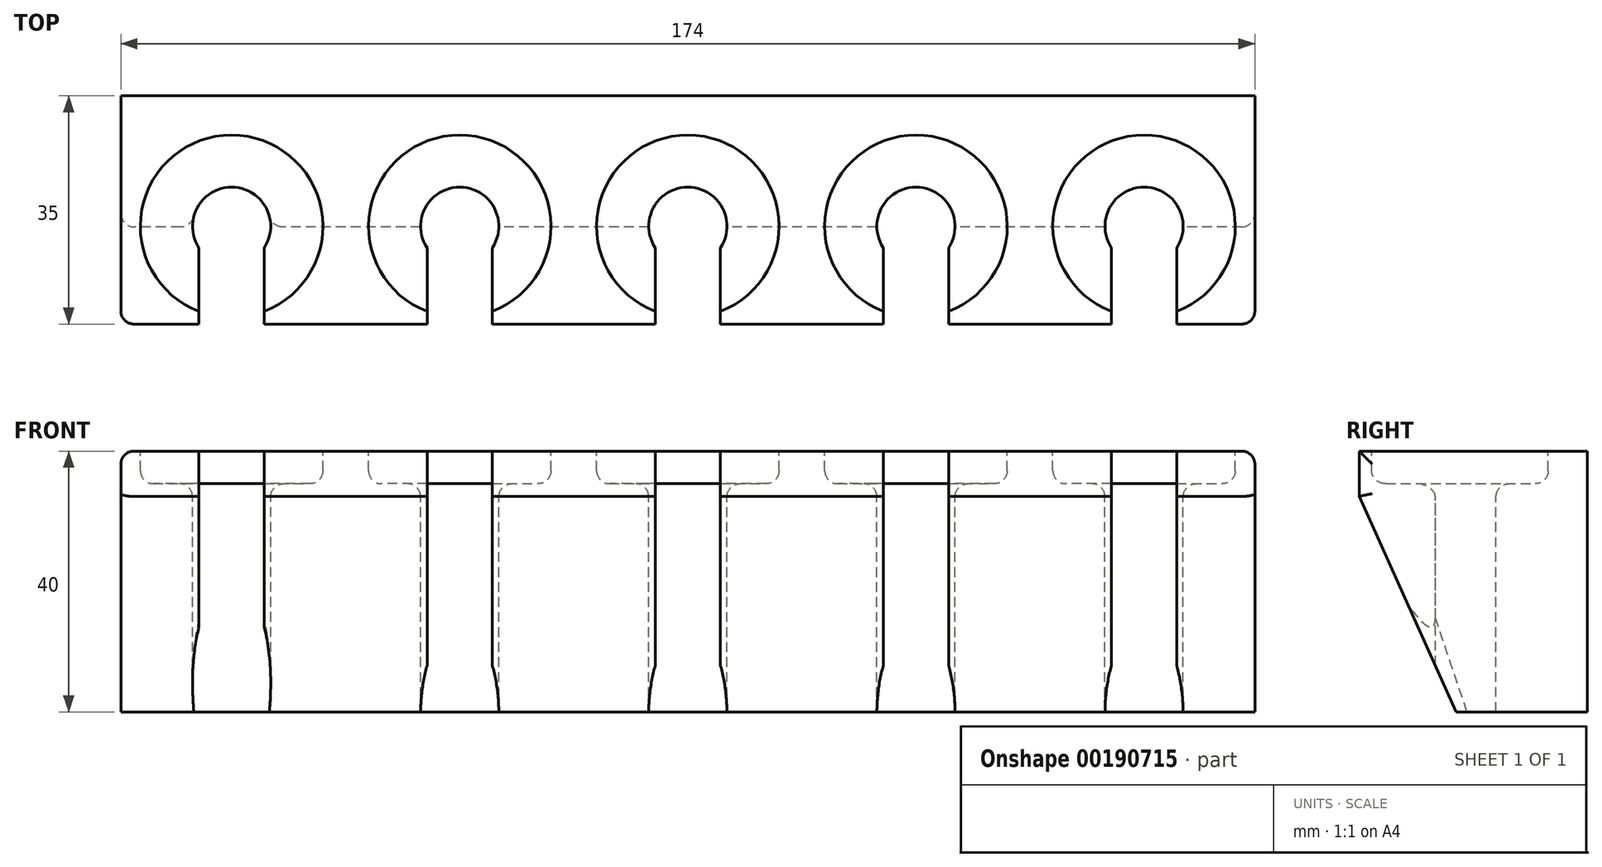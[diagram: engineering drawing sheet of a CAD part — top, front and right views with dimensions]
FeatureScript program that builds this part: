
annotation { "Feature Type Name" : "Feature", "Feature Type Description" : "" }
export const myFeature = defineFeature(function(context is Context, id is Id, definition is map)
    precondition{}
    {
        {
            var Q0;
            Q0=qCreatedBy(makeId("Right.planeOp"),FACE);
            var sketch = newSketch(context, id + "F0", { "sketchPlane" : qUnion([Q0])});
            skLineSegment(sketch, "E0", {"start": v(0, 0) * mm, "end": v(0, -40) * mm});
            skLineSegment(sketch, "E1", {"start": v(-35, 0) * mm, "end": v(0, 0) * mm});
            skLineSegment(sketch, "E2", {"start": v(-20.11, -40) * mm, "end": v(0, -40) * mm});
            skLineSegment(sketch, "E3", {"start": v(-35, 0) * mm, "end": v(-35, -6.93) * mm});
            skLineSegment(sketch, "E4", {"start": v(-35, -6.93) * mm, "end": v(-20.11, -40) * mm});
            skSolve(sketch);
        }
        {
            var Q0;
            Q0=makeQuery(id+"F0.imprint","IMPRINT",FACE,{"disambiguationData":[TD([[makeQuery(id+"F0.imprint","IMPRINT",EDGE,{"derivedFrom":sQuery(id+"F0.wireOp",EDGE,"E0")}),-1.0]])]});
            extrude(context, id + "F1", {"entities" : qUnion([Q0]), "depth" : 174 * mm});
        }
        {
            var Q0;
            Q0=makeQuery(id+"F1.opExtrude","SWEPT_FACE",FACE,{"disambiguationData":[OSD([sQuery(id+"F0.wireOp",EDGE,"E1")])]});
            var sketch = newSketch(context, id + "F2", { "sketchPlane" : qUnion([Q0])});
            skLineSegment(sketch, "E5", {"start": v(-22.77, -20) * mm, "end": v(173.52, -20) * mm, "construction": true});
            skLineSegment(sketch, "E6", {"start": v(17, 14.3) * mm, "end": v(17, -43.16) * mm, "construction": true});
            skArc(sketch, "E7", {"start": v(22, -23.32) * mm, "mid": v(17, -14) * mm, "end": v(12, -23.32) * mm});
            skLineSegment(sketch, "E8.direction1", {"start": v(17, -20) * mm, "end": v(18, -20) * mm, "construction": true});
            skLineSegment(sketch, "E9", {"start": v(12, -23.32) * mm, "end": v(12, -35) * mm});
            skLineSegment(sketch, "E10", {"start": v(12, -35) * mm, "end": v(22, -35) * mm});
            skLineSegment(sketch, "E11", {"start": v(22, -35) * mm, "end": v(22, -23.32) * mm});
            skArc(sketch, "E12.1.0.0", {"start": v(57, -23.32) * mm, "mid": v(52, -14) * mm, "end": v(47, -23.32) * mm});
            skLineSegment(sketch, "E12.1.0.1", {"start": v(47, -23.32) * mm, "end": v(47, -35) * mm});
            skLineSegment(sketch, "E12.1.0.2", {"start": v(47, -35) * mm, "end": v(57, -35) * mm});
            skLineSegment(sketch, "E12.1.0.3", {"start": v(57, -35) * mm, "end": v(57, -23.32) * mm});
            skArc(sketch, "E12.2.0.0", {"start": v(92, -23.32) * mm, "mid": v(87, -14) * mm, "end": v(82, -23.32) * mm});
            skLineSegment(sketch, "E12.2.0.1", {"start": v(82, -23.32) * mm, "end": v(82, -35) * mm});
            skLineSegment(sketch, "E12.2.0.2", {"start": v(82, -35) * mm, "end": v(92, -35) * mm});
            skLineSegment(sketch, "E12.2.0.3", {"start": v(92, -35) * mm, "end": v(92, -23.32) * mm});
            skArc(sketch, "E12.3.0.0", {"start": v(127, -23.32) * mm, "mid": v(122, -14) * mm, "end": v(117, -23.32) * mm});
            skLineSegment(sketch, "E12.3.0.1", {"start": v(117, -23.32) * mm, "end": v(117, -35) * mm});
            skLineSegment(sketch, "E12.3.0.2", {"start": v(117, -35) * mm, "end": v(127, -35) * mm});
            skLineSegment(sketch, "E12.3.0.3", {"start": v(127, -35) * mm, "end": v(127, -23.32) * mm});
            skArc(sketch, "E12.4.0.0", {"start": v(162, -23.32) * mm, "mid": v(157, -14) * mm, "end": v(152, -23.32) * mm});
            skLineSegment(sketch, "E12.4.0.1", {"start": v(152, -23.32) * mm, "end": v(152, -35) * mm});
            skLineSegment(sketch, "E12.4.0.2", {"start": v(152, -35) * mm, "end": v(162, -35) * mm});
            skLineSegment(sketch, "E12.4.0.3", {"start": v(162, -35) * mm, "end": v(162, -23.32) * mm});
            skLineSegment(sketch, "E12.direction1", {"start": v(12, -35) * mm, "end": v(47, -35) * mm, "construction": true});
            skSolve(sketch);
        }
        {
            var Q0;
            Q0 = qSketchRegion(id + "F2", true);
            extrude(context, id + "F3", {"entities" : qUnion([Q0]), "operationType" : NewBodyOperationType.REMOVE, "endBound" : BoundingType.THROUGH_ALL, "oppositeDirection" : true, "depth" : 25 * mm});
        }
        {
            var Q0;
            Q0=makeQuery(id+"F2.imprint","IMPRINT",FACE,{"disambiguationData":[TD([[makeQuery(id+"F2.imprint","IMPRINT",EDGE,{"derivedFrom":sQuery(id+"F2.wireOp",EDGE,"E7")}),-1.0]])]});
            var sketch = newSketch(context, id + "F4", { "sketchPlane" : qUnion([Q0])});
            skPoint(sketch, "E13.0", {"position": v(17, -20) * mm});
            skCircle(sketch, "E14", {"center": v(17, -20) * mm, "radius": 14 * mm});
            skCircle(sketch, "E15.1.0.0", {"center": v(52, -20) * mm, "radius": 14 * mm});
            skCircle(sketch, "E15.2.0.0", {"center": v(87, -20) * mm, "radius": 14 * mm});
            skCircle(sketch, "E15.3.0.0", {"center": v(122, -20) * mm, "radius": 14 * mm});
            skCircle(sketch, "E15.4.0.0", {"center": v(157, -20) * mm, "radius": 14 * mm});
            skLineSegment(sketch, "E15.direction1", {"start": v(17, -20) * mm, "end": v(52, -20) * mm, "construction": true});
            skSolve(sketch);
        }
        {
            var Q0;
            Q0 = qSketchRegion(id + "F4", true);
            extrude(context, id + "F5", {"entities" : qUnion([Q0]), "operationType" : NewBodyOperationType.REMOVE, "oppositeDirection" : true, "depth" : 5 * mm});
        }
        {
            var Q0;
            Q0=makeQuery(id+"F3.boolean.opBoolean","COPY",EDGE,{"derivedFrom":makeQuery(id+"F3.opExtrude","CAP_EDGE",EDGE,{"disambiguationData":[OSD([sQuery(id+"F2.wireOp",EDGE,"E8.1.0.0")])],"isStart":true})});
            var Q1;
            Q1=makeQuery(id+"F3.boolean.opBoolean","COPY",EDGE,{"derivedFrom":makeQuery(id+"F3.opExtrude","CAP_EDGE",EDGE,{"disambiguationData":[OSD([sQuery(id+"F2.wireOp",EDGE,"E8.2.0.0")])],"isStart":true})});
            var Q2;
            Q2=makeQuery(id+"F3.boolean.opBoolean","COPY",EDGE,{"derivedFrom":makeQuery(id+"F3.opExtrude","CAP_EDGE",EDGE,{"disambiguationData":[OSD([sQuery(id+"F2.wireOp",EDGE,"E8.3.0.0")])],"isStart":true})});
            var Q3;
            Q3=makeQuery(id+"F3.boolean.opBoolean","COPY",EDGE,{"derivedFrom":makeQuery(id+"F3.opExtrude","CAP_EDGE",EDGE,{"disambiguationData":[OSD([sQuery(id+"F2.wireOp",EDGE,"E8.4.0.0")])],"isStart":true})});
            var Q4;
            Q4=makeQuery(id+"F3.boolean.opBoolean","INTERSECT",EDGE,{"derivedFrom":[makeQuery(id+"F1.opExtrude","SWEPT_FACE",FACE,{"disambiguationData":[OSD([sQuery(id+"F0.wireOp",EDGE,"E4")])]}),makeQuery(id+"F3.opExtrude","SWEPT_FACE",FACE,{"disambiguationData":[OSD([sQuery(id+"F2.wireOp",EDGE,"E7")])]})]});
            var Q5;
            Q5=makeQuery(id+"F3.boolean.opBoolean","INTERSECT",EDGE,{"derivedFrom":[makeQuery(id+"F1.opExtrude","SWEPT_FACE",FACE,{"disambiguationData":[OSD([sQuery(id+"F0.wireOp",EDGE,"E4")])]}),makeQuery(id+"F3.opExtrude","SWEPT_FACE",FACE,{"disambiguationData":[OSD([sQuery(id+"F2.wireOp",EDGE,"E8.1.0.0")])]})]});
            var Q6;
            Q6=makeQuery(id+"F3.boolean.opBoolean","INTERSECT",EDGE,{"derivedFrom":[makeQuery(id+"F1.opExtrude","SWEPT_FACE",FACE,{"disambiguationData":[OSD([sQuery(id+"F0.wireOp",EDGE,"E4")])]}),makeQuery(id+"F3.opExtrude","SWEPT_FACE",FACE,{"disambiguationData":[OSD([sQuery(id+"F2.wireOp",EDGE,"E8.2.0.0")])]})]});
            var Q7;
            Q7=makeQuery(id+"F3.boolean.opBoolean","INTERSECT",EDGE,{"derivedFrom":[makeQuery(id+"F1.opExtrude","SWEPT_FACE",FACE,{"disambiguationData":[OSD([sQuery(id+"F0.wireOp",EDGE,"E4")])]}),makeQuery(id+"F3.opExtrude","SWEPT_FACE",FACE,{"disambiguationData":[OSD([sQuery(id+"F2.wireOp",EDGE,"E8.3.0.0")])]})]});
            var Q8;
            Q8=makeQuery(id+"F1.opExtrude","CAP_EDGE",EDGE,{"disambiguationData":[OSD([sQuery(id+"F0.wireOp",EDGE,"E3")])],"isStart":true});
            var Q9;
            Q9=makeQuery(id+"F1.opExtrude","CAP_EDGE",EDGE,{"disambiguationData":[OSD([sQuery(id+"F0.wireOp",EDGE,"E3")])],"isStart":false});
            var Q10;
            Q10=makeQuery(id+"F1.opExtrude","CAP_EDGE",EDGE,{"disambiguationData":[OSD([sQuery(id+"F0.wireOp",EDGE,"E1")])],"isStart":true});
            var Q11;
            Q11=makeQuery(id+"F1.opExtrude","CAP_EDGE",EDGE,{"disambiguationData":[OSD([sQuery(id+"F0.wireOp",EDGE,"E1")])],"isStart":false});
            var Q12;
            Q12=makeQuery(id+"F5.boolean.opBoolean","COPY",EDGE,{"derivedFrom":makeQuery(id+"F5.opExtrude","CAP_EDGE",EDGE,{"disambiguationData":[OSD([sQuery(id+"F4.wireOp",EDGE,"E14")])],"isStart":true})});
            var Q13;
            Q13=makeQuery(id+"F5.boolean.opBoolean","COPY",EDGE,{"derivedFrom":makeQuery(id+"F5.opExtrude","CAP_EDGE",EDGE,{"disambiguationData":[OSD([sQuery(id+"F4.wireOp",EDGE,"E15.1.0.0")])],"isStart":true})});
            var Q14;
            Q14=makeQuery(id+"F5.boolean.opBoolean","COPY",EDGE,{"derivedFrom":makeQuery(id+"F5.opExtrude","CAP_EDGE",EDGE,{"disambiguationData":[OSD([sQuery(id+"F4.wireOp",EDGE,"E15.2.0.0")])],"isStart":true})});
            var Q15;
            Q15=makeQuery(id+"F5.boolean.opBoolean","COPY",EDGE,{"derivedFrom":makeQuery(id+"F5.opExtrude","CAP_EDGE",EDGE,{"disambiguationData":[OSD([sQuery(id+"F4.wireOp",EDGE,"E15.3.0.0")])],"isStart":true})});
            var Q16;
            Q16=makeQuery(id+"F5.boolean.opBoolean","COPY",EDGE,{"derivedFrom":makeQuery(id+"F5.opExtrude","CAP_EDGE",EDGE,{"disambiguationData":[OSD([sQuery(id+"F4.wireOp",EDGE,"E15.4.0.0")])],"isStart":true})});
            var Q17;
            Q17=makeQuery(id+"F1.opExtrude","CAP_EDGE",EDGE,{"disambiguationData":[OSD([sQuery(id+"F0.wireOp",EDGE,"E4")])],"isStart":true});
            var Q18;
            Q18=makeQuery(id+"F1.opExtrude","CAP_EDGE",EDGE,{"disambiguationData":[OSD([sQuery(id+"F0.wireOp",EDGE,"E4")])],"isStart":false});
            var Q19;
            Q19=makeQuery(id+"F5.boolean.opBoolean","COPY",EDGE,{"derivedFrom":makeQuery(id+"F5.opExtrude","CAP_EDGE",EDGE,{"disambiguationData":[OSD([sQuery(id+"F4.wireOp",EDGE,"E14")])],"isStart":false})});
            var Q20;
            Q20=makeQuery(id+"F5.boolean.opBoolean","COPY",EDGE,{"derivedFrom":makeQuery(id+"F5.opExtrude","CAP_EDGE",EDGE,{"disambiguationData":[OSD([sQuery(id+"F4.wireOp",EDGE,"E15.1.0.0")])],"isStart":false})});
            var Q21;
            Q21=makeQuery(id+"F5.boolean.opBoolean","COPY",EDGE,{"derivedFrom":makeQuery(id+"F5.opExtrude","CAP_EDGE",EDGE,{"disambiguationData":[OSD([sQuery(id+"F4.wireOp",EDGE,"E15.2.0.0")])],"isStart":false})});
            var Q22;
            Q22=makeQuery(id+"F5.boolean.opBoolean","COPY",EDGE,{"derivedFrom":makeQuery(id+"F5.opExtrude","CAP_EDGE",EDGE,{"disambiguationData":[OSD([sQuery(id+"F4.wireOp",EDGE,"E15.3.0.0")])],"isStart":false})});
            var Q23;
            Q23=makeQuery(id+"F5.boolean.opBoolean","COPY",EDGE,{"derivedFrom":makeQuery(id+"F5.opExtrude","CAP_EDGE",EDGE,{"disambiguationData":[OSD([sQuery(id+"F4.wireOp",EDGE,"E15.4.0.0")])],"isStart":false})});
            var Q24;
            Q24=makeQuery(id+"F5.boolean.opBoolean","INTERSECT",EDGE,{"derivedFrom":[makeQuery(id+"F3.boolean.opBoolean","COPY",FACE,{"derivedFrom":makeQuery(id+"F3.opExtrude","SWEPT_FACE",FACE,{"disambiguationData":[OSD([sQuery(id+"F2.wireOp",EDGE,"E7")])]})}),makeQuery(id+"F5.opExtrude","CAP_FACE",FACE,{"disambiguationData":[OSD([sQuery(id+"F4.wireOp",EDGE,"E14")])],"isStart":false})]});
            var Q25;
            Q25=makeQuery(id+"F5.boolean.opBoolean","INTERSECT",EDGE,{"derivedFrom":[makeQuery(id+"F3.boolean.opBoolean","COPY",FACE,{"derivedFrom":makeQuery(id+"F3.opExtrude","SWEPT_FACE",FACE,{"disambiguationData":[OSD([sQuery(id+"F2.wireOp",EDGE,"E12.1.0.0")])]})}),makeQuery(id+"F5.opExtrude","CAP_FACE",FACE,{"disambiguationData":[OSD([sQuery(id+"F4.wireOp",EDGE,"E15.1.0.0")])],"isStart":false})]});
            var Q26;
            Q26=makeQuery(id+"F5.boolean.opBoolean","INTERSECT",EDGE,{"derivedFrom":[makeQuery(id+"F3.boolean.opBoolean","COPY",FACE,{"derivedFrom":makeQuery(id+"F3.opExtrude","SWEPT_FACE",FACE,{"disambiguationData":[OSD([sQuery(id+"F2.wireOp",EDGE,"E12.2.0.0")])]})}),makeQuery(id+"F5.opExtrude","CAP_FACE",FACE,{"disambiguationData":[OSD([sQuery(id+"F4.wireOp",EDGE,"E15.2.0.0")])],"isStart":false})]});
            var Q27;
            Q27=makeQuery(id+"F5.boolean.opBoolean","INTERSECT",EDGE,{"derivedFrom":[makeQuery(id+"F3.boolean.opBoolean","COPY",FACE,{"derivedFrom":makeQuery(id+"F3.opExtrude","SWEPT_FACE",FACE,{"disambiguationData":[OSD([sQuery(id+"F2.wireOp",EDGE,"E12.3.0.0")])]})}),makeQuery(id+"F5.opExtrude","CAP_FACE",FACE,{"disambiguationData":[OSD([sQuery(id+"F4.wireOp",EDGE,"E15.3.0.0")])],"isStart":false})]});
            var Q28;
            Q28=makeQuery(id+"F5.boolean.opBoolean","INTERSECT",EDGE,{"derivedFrom":[makeQuery(id+"F3.boolean.opBoolean","COPY",FACE,{"derivedFrom":makeQuery(id+"F3.opExtrude","SWEPT_FACE",FACE,{"disambiguationData":[OSD([sQuery(id+"F2.wireOp",EDGE,"E12.4.0.0")])]})}),makeQuery(id+"F5.opExtrude","CAP_FACE",FACE,{"disambiguationData":[OSD([sQuery(id+"F4.wireOp",EDGE,"E15.4.0.0")])],"isStart":false})]});
            fillet(context, id + "F6", {"entities" : qUnion([Q0, Q1, Q2, Q3, Q4, Q5, Q6, Q7, Q8, Q9, Q10, Q11, Q12, Q13, Q14, Q15, Q16, Q17, Q18, Q19, Q20, Q21, Q22, Q23, Q24, Q25, Q26, Q27, Q28]), "radius" : 2 * mm, "tangentPropagation" : true, "allowEdgeOverflow" : false});
        }
    });
